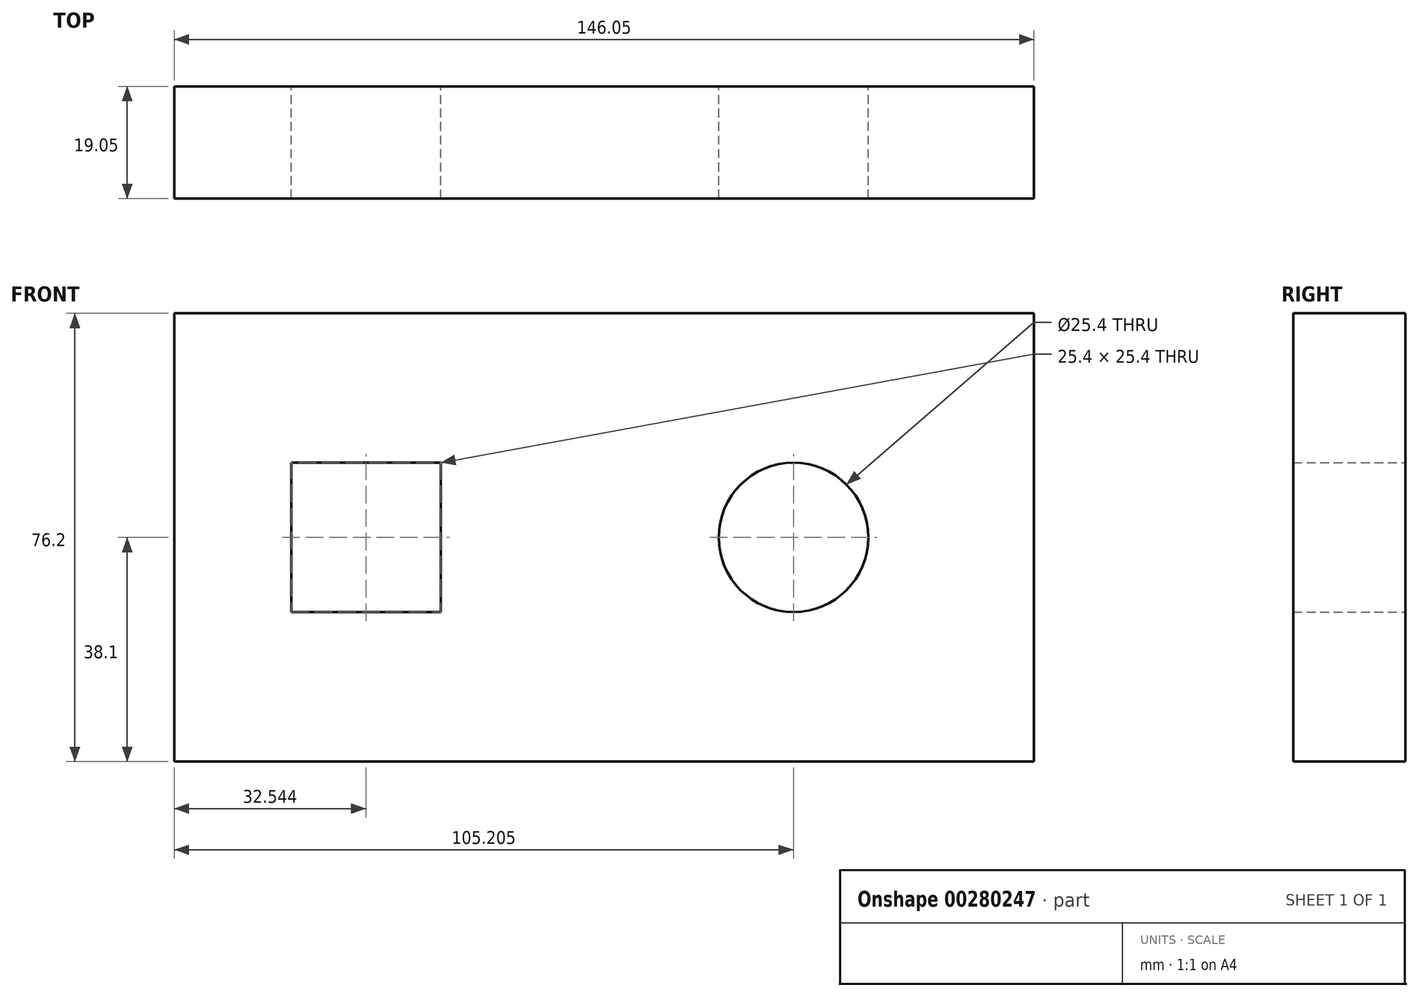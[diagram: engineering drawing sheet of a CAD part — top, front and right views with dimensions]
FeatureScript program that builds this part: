
annotation { "Feature Type Name" : "Feature", "Feature Type Description" : "" }
export const myFeature = defineFeature(function(context is Context, id is Id, definition is map)
    precondition{}
    {
        {
            var Q0;
            Q0=qCreatedBy(makeId("Front.planeOp"),FACE);
            var sketch = newSketch(context, id + "F0", { "sketchPlane" : qUnion([Q0])});
            skLineSegment(sketch, "E0.bottom", {"start": v(0, 0) * mm, "end": v(-146.05, 0) * mm});
            skLineSegment(sketch, "E0.top", {"start": v(0, 76.2) * mm, "end": v(-146.05, 76.2) * mm});
            skLineSegment(sketch, "E0.left", {"start": v(0, 0) * mm, "end": v(0, 76.2) * mm});
            skLineSegment(sketch, "E0.right", {"start": v(-146.05, 0) * mm, "end": v(-146.05, 76.2) * mm});
            skCircle(sketch, "E1", {"center": v(-40.84, 38.1) * mm, "radius": 12.7 * mm});
            skLineSegment(sketch, "E2.bottom", {"start": v(-100.8, 25.4) * mm, "end": v(-126.2, 25.4) * mm});
            skLineSegment(sketch, "E2.top", {"start": v(-100.8, 50.8) * mm, "end": v(-126.2, 50.8) * mm});
            skLineSegment(sketch, "E2.left", {"start": v(-100.8, 25.4) * mm, "end": v(-100.8, 50.8) * mm});
            skLineSegment(sketch, "E2.right", {"start": v(-126.2, 25.4) * mm, "end": v(-126.2, 50.8) * mm});
            skSolve(sketch);
        }
        {
            var Q0;
            Q0 = qSketchRegion(id + "F0", true);
            extrude(context, id + "F1", {"entities" : qUnion([Q0]), "depth" : 19.05 * mm});
        }
    });
